# Revit family: QF_MACOM_ME7xx-x
name_source: partatom
category: Equipamento especial
units: mm (PartAtom-declared; Revit-internal decimal feet)

## family parameters
Com base no plano de trabalho = Não
Compartilhado = Não
Corte com vazios quando carregada = Não
Cota do conector redondo = Utilizar diâmetro
Número OmniClass = 23.40.40.14.24
Ponto de cálculo do ambiente = Não
Sempre na vertical = Sim
Tipo de parte = Normal
Título OmniClass = Food Dispensing Equipment

## types (8) — shared parameters
Depth = 645 mm
Door 2 = 360 mm
Elevação padrão = 0 mm
Fabricante = MACOM
Height = 655 mm
URL = https://www.acosmacom.com.br

## per-type parameters (varying)
| type | Descrição | Door 3 | Door 4 | Dr | Dr2 | Dr3 | Dr4 | Foot w/ 1440 | Foot w/ 1440 Width | Show Clearance | Volume | Weight | Width |
| ME74-P | MÓDULO BASE DE ESCOSTO COM PORTA 1440 | 720 mm | 1080 mm | Sim | Sim | Sim | Sim | Sim | 720 mm | Sim | 0,62 m³ | 36,00 kg | 1440 mm |
| ME74-A | MÓDULO BASE DE ESCOSTO ABERTO 1440 | 720 mm | 1080 mm | Não | Não | Não | Não | Sim | 720 mm | Não | 0,62 m³ | 36,00 kg | 1440 mm |
| ME73-P | MÓDULO BASE DE ESCOSTO COM PORTA 1080 | 720 mm | 720 mm | Sim | Sim | Não | Sim | Não | 65 mm | Sim | 0,46 m³ | 28,00 kg | 1080 mm |
| ME73-A | MÓDULO BASE DE ESCOSTO ABERTO 1080 | 720 mm | 720 mm | Não | Não | Não | Não | Não | 65 mm | Não | 0,46 m³ | 28,00 kg | 1080 mm |
| ME72-P | MÓDULO BASE DE ESCOSTO COM PORTA 720 | 720 mm | 720 mm | Não | Não | Sim | Sim | Não | 65 mm | Sim | 0,31 m³ | 23,00 kg | 720 mm |
| ME71-P | MÓDULO BASE DE ESCOSTO COM PORTA 360 | 360 mm | 360 mm | Não | Não | Não | Sim | Não | 65 mm | Sim | 0,15 m³ | 16,00 kg | 360 mm |
| ME71-A | MÓDULO BASE DE ESCOSTO ABERTO 360 | 360 mm | 360 mm | Não | Não | Não | Não | Não | 65 mm | Não | 0,15 m³ | 16,00 kg | 360 mm |
| ME72-A | MÓDULO BASE DE ESCOSTO ABERTO 720 | 360 mm | 720 mm | Não | Não | Não | Não | Não | 65 mm | Não | 0,31 m³ | 23,00 kg | 720 mm |

note: column(s) folded — value = type name in every type: Modelo

## geometry (parser evidence)
native form markers: Sweep x7
no freeform markers — native parametric forms only
